# Revit family: RN 90095 Optifitt-Serra-Schlauchstutzen
name_source: partatom
category: Rohrformteile
units: mm (PartAtom-declared; Revit-internal decimal feet)

## family parameters
Arbeitsebenenbasiert = Nein
Beim Laden mit Abzugskörper schneiden = Nein
Bemaßung runder Anschluss = Durchmesser verwenden
Gemeinsam genutzt = Nein
Immer vertikal = Ja
Teiletyp = Verbindung

## types (3) — shared parameters
1.010.00.2 Blattnummer der Richtlinie = 29
1.010.00.3 Ausgabedatum (Monat) der Richtlinie = 201308
1.010.00.4 Herstellername = R. Nussbaum AG
1.010.00.5 Revisionsdatum der Datei = 20190521
1.010.00.6 Webadresse des Herstellers = http://www.nussbaum.ch
1.100.00.4 Produktbezeichnung = Versorgung
1.110.00.2 Index = 3
1.110.00.4 Produktbezeichnung = Optifitt-Serra
1.960/3L.00.8 Link (URL) = https://www.nussbaum.ch
29.700.00.4 Produktname = Optifitt-Serra-Schlauchstutzen, mit Schlauchtülle
29.700.00.5 Produktkennung = 2
29.700.00.6 Querschnittsform = 1
29.700.00.7 Nennweitensystem = DN
29.700.00.8 Nenndrucksystem = PN
29.710.02.4 Nenndruck = 16
29.710.02.5 max. zul. Überdruck [hPa] = 1600
29.710.02.7 max. zul. Dauer-Betriebsdruck [hPa] = 1600
29.710.02.9 max. zul. Dauer-Betriebstemperatur [°C] = 90
Connector Visibility = Nein
EnclosingSpace Visibility = Nein
Hersteller = R. Nussbaum AG
URL = https://www.nussbaum.ch

## per-type parameters (varying)
| type | 1.800.00.3 TGA-Nummer | 1.800.00.4 Kommentarfeld | 1.810.00.3 Hersteller-Bestellnummer | 1.810.00.4 DATANORM-Nummer | 1.810.00.6 GTIN-Nummer | 29.710.02.10 Formstück-Gewicht [kg] | 29.710.02.3 Benennung | CONNECTOR0_DIAMETER_dX_0r | CONNECTOR0_dX_01 | CONNECTOR0_ref_dX | CONNECTOR1_DIAMETER_dX_0r | CONNECTOR1_dX_00 | CONNECTOR1_dX_01 | CONNECTOR1_ref_dX | Modell | R. Nussbaum AG 90095.24 de Visibility | R. Nussbaum AG 90095.27 de Visibility | R. Nussbaum AG 90095.33 de Visibility | Typenkommentare |
| DN=25 | 01900300000000000000000000000000000000000000000033000000000000000003 | 90095.33, Optifitt-Serra-Schlauchstutzen, mit Schlauchtülle, DN=25, L=71, R=1 | 90095.33 | 90095.33 | 7612945680754 | 0.223 | Optifitt-Serra-Schlauchstutzen, mit Schlauchtülle, DN=25, L=71, R=1 | 25 mm  [stored 0.082021 ft] | 17 mm  [stored 0.0557743 ft] | 17 mm  [stored 0.0557743 ft] | 20 mm | 51 mm | 71 mm | 51 mm | 90095.33 | Nein | Nein | Ja | Optifitt-Serra-Schlauchstutzen  DN=25 |
| DN=20 | 01900300000000000000000000000000000000000000000033000000000000000002 | 90095.27, Optifitt-Serra-Schlauchstutzen, mit Schlauchtülle, DN=20, L=68, R=¾ | 90095.27 | 90095.27 | 7612945680747 | 0.128 | Optifitt-Serra-Schlauchstutzen, mit Schlauchtülle, DN=20, L=68, R=¾ | 20 mm | 15 mm | 15 mm | 15 mm | 48 mm | 68 mm | 48 mm | 90095.27 | Nein | Ja | Nein | Optifitt-Serra-Schlauchstutzen  DN=20 |
| DN=15 | 01900300000000000000000000000000000000000000000033000000000000000001 | 90095.24, Optifitt-Serra-Schlauchstutzen, mit Schlauchtülle, DN=15, L=64, R=½ | 90095.24 | 90095.24 | 7612945680730 | 0.074 | Optifitt-Serra-Schlauchstutzen, mit Schlauchtülle, DN=15, L=64, R=½ | 15 mm | 13 mm | 13 mm | 10 mm  [stored 0.0328084 ft] | 44 mm | 64 mm | 44 mm | 90095.24 | Ja | Nein | Nein | Optifitt-Serra-Schlauchstutzen  DN=15 |

note: [stored X ft] marks values corroborated as IEEE doubles in the binary element streams (Revit-internal decimal feet)

## geometry (parser evidence)
native form markers: Sweep x2
no freeform markers — native parametric forms only
